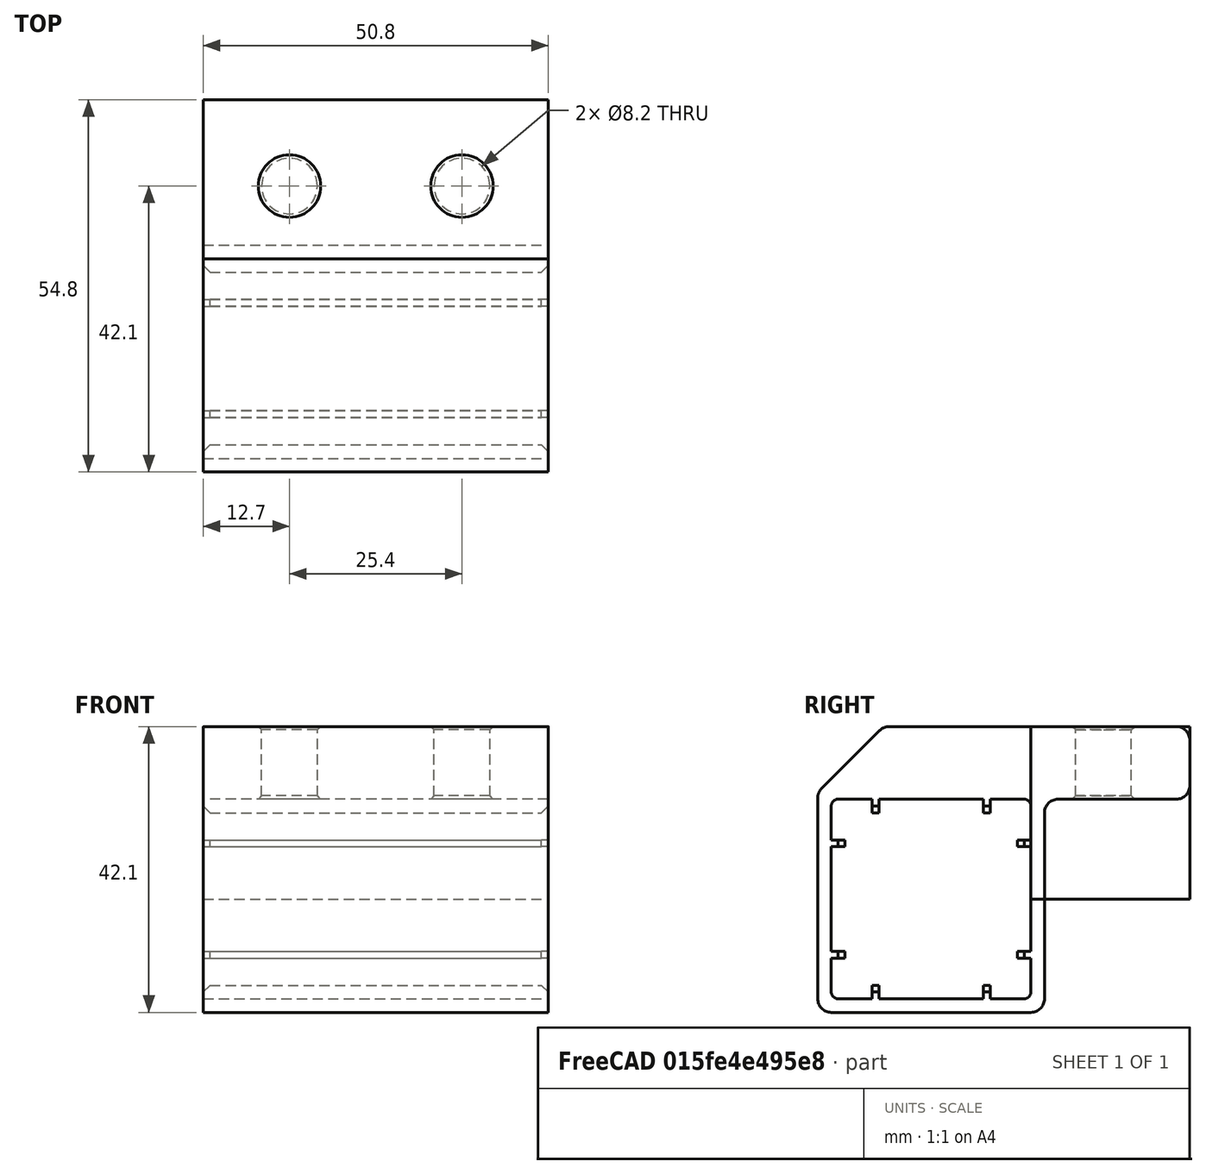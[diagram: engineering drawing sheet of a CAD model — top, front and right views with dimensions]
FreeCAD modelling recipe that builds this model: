
FCSTD DOCUMENT  (FreeCAD 0.16RUnknown)
Label: linear-bearing
License: All rights reserved
LicenseURL: http://en.wikipedia.org/wiki/All_rights_reserved
objects: Part::Box×12, PartDesign::Fillet×3, Part::Cut×3, Part::Chamfer×3, Part::Fillet×3, Part::MultiFuse×2, Part::Cylinder×2
note: 28 computed .brp shape members not serialized (recipe doc carries the construction recipe); baked Part::Feature solids carry a one-line shape summary decoded from their .brp

FEATURE [Part::Box] Box  label="Cube"
  Height = 29.4
  Length = 52
  Placement = pos=(-1,2,2) rot=(0,0,1;0rad)
  Width = 29.4
FEATURE [Part::Box] Box001  label="Cube001"
  Height = 33.4
  Length = 50.8
  Width = 33.4
FEATURE [PartDesign::Fillet] Fillet
  Base = -> Box001 [Edge11,Edge9,Edge10,Edge12]
  Radius = 2
FEATURE [PartDesign::Fillet] Fillet001
  Base = -> Box [Edge10,Edge9,Edge12,Edge11]
  Placement = pos=(-1,2,2) rot=(0,0,1;0rad)
  Radius = 1
FEATURE [Part::Cut] Cut
  Base = -> Fillet
  Tool = -> Fillet001
FEATURE [Part::Box] Box002  label="Cube002"
  Height = 1
  Length = 50.8
  Placement = pos=(0,0,8) rot=(0,0,1;0rad)
  Width = 4
FEATURE [Part::Box] Box003  label="Cube003"
  Height = 1
  Length = 50.8
  Placement = pos=(0,0,24.4) rot=(0,0,1;0rad)
  Width = 4
FEATURE [Part::Box] Box004  label="Cube004"
  Height = 1
  Length = 50.8
  Placement = pos=(0,29.4,8) rot=(0,0,1;0rad)
  Width = 4
FEATURE [Part::Box] Box005  label="Cube005"
  Height = 1
  Length = 50.8
  Placement = pos=(0,29.4,24.4) rot=(0,0,1;0rad)
  Width = 4
FEATURE [Part::Box] Box006  label="Cube006"
  Height = 4
  Length = 50.8
  Placement = pos=(0,8,0) rot=(0,0,1;0rad)
  Width = 1
FEATURE [Part::Box] Box007  label="Cube007"
  Height = 4
  Length = 50.8
  Placement = pos=(0,24.4,0) rot=(0,0,1;0rad)
  Width = 1
FEATURE [Part::Box] Box008  label="Cube008"
  Height = 4
  Length = 50.8
  Placement = pos=(0,24.4,29.4) rot=(0,0,1;0rad)
  Width = 1
FEATURE [Part::Box] Box009  label="Cube009"
  Height = 4
  Length = 50.8
  Placement = pos=(0,8,29.4) rot=(0,0,1;0rad)
  Width = 1
FEATURE [Part::Box] Box010  label="Cube010"
  Height = 10.7
  Length = 50.8
  Placement = pos=(0,0,31.4) rot=(0,0,1;0rad)
  Width = 54.8
FEATURE [Part::Box] Box011  label="Cube011"
  Height = 25.4
  Length = 50.8
  Placement = pos=(0,31.4,16.7) rot=(0,0,1;0rad)
  Width = 23.4
FEATURE [Part::MultiFuse] Fusion
  Shapes = -> [Cut,Box010]
FEATURE [PartDesign::Fillet] Fillet002
  Base = -> Fusion [Edge19]
  Radius = 2
FEATURE [Part::Cylinder] Cylinder
  Angle = 360
  Height = 14
  Placement = pos=(12.7,42.1,30) rot=(0,0,1;0rad)
  Radius = 4.1
FEATURE [Part::Cylinder] Cylinder001
  Angle = 360
  Height = 14
  Placement = pos=(38.1,42.1,30) rot=(0,0,1;0rad)
  Radius = 4.1
FEATURE [Part::Chamfer] Chamfer
  Base = -> Fillet002
  Edges = 1 edges r=9.7: [Edge31]
FEATURE [Part::Fillet] Fillet003
  Base = -> Chamfer
  Edges = 1 edges r=2: [Edge10]
FEATURE [Part::Fillet] Fillet004
  Base = -> Fillet003
  Edges = 1 edges r=2: [Edge18]
FEATURE [Part::Fillet] Fillet005
  Base = -> Fillet004
  Edges = 2 edges r=2: [Edge21,Edge26]
FEATURE [Part::Cut] Cut001
  Base = -> Fillet005
  Tool = -> Cylinder
FEATURE [Part::Cut] Cut002
  Base = -> Cut001
  Tool = -> Cylinder001
FEATURE [Part::MultiFuse] Fusion001
  Shapes = -> [Cut002,Box005,Box008,Box009,Box003,Box002,Box006,Box007,Box004]
FEATURE [Part::Chamfer] Chamfer001
  Base = -> Fusion001
  Edges = 4 edges r=0.5: [Edge174,Edge175,Edge182,Edge183]
FEATURE [Part::Chamfer] Chamfer002
  Base = -> Chamfer001
  Edges = 16 edges r=1: [Edge110,Edge113,Edge124,Edge127,Edge137,Edge152,Edge168,Edge175,Edge192,Edge208,Edge228,Edge239,Edge253,Edge269,Edge279,Edge281]
